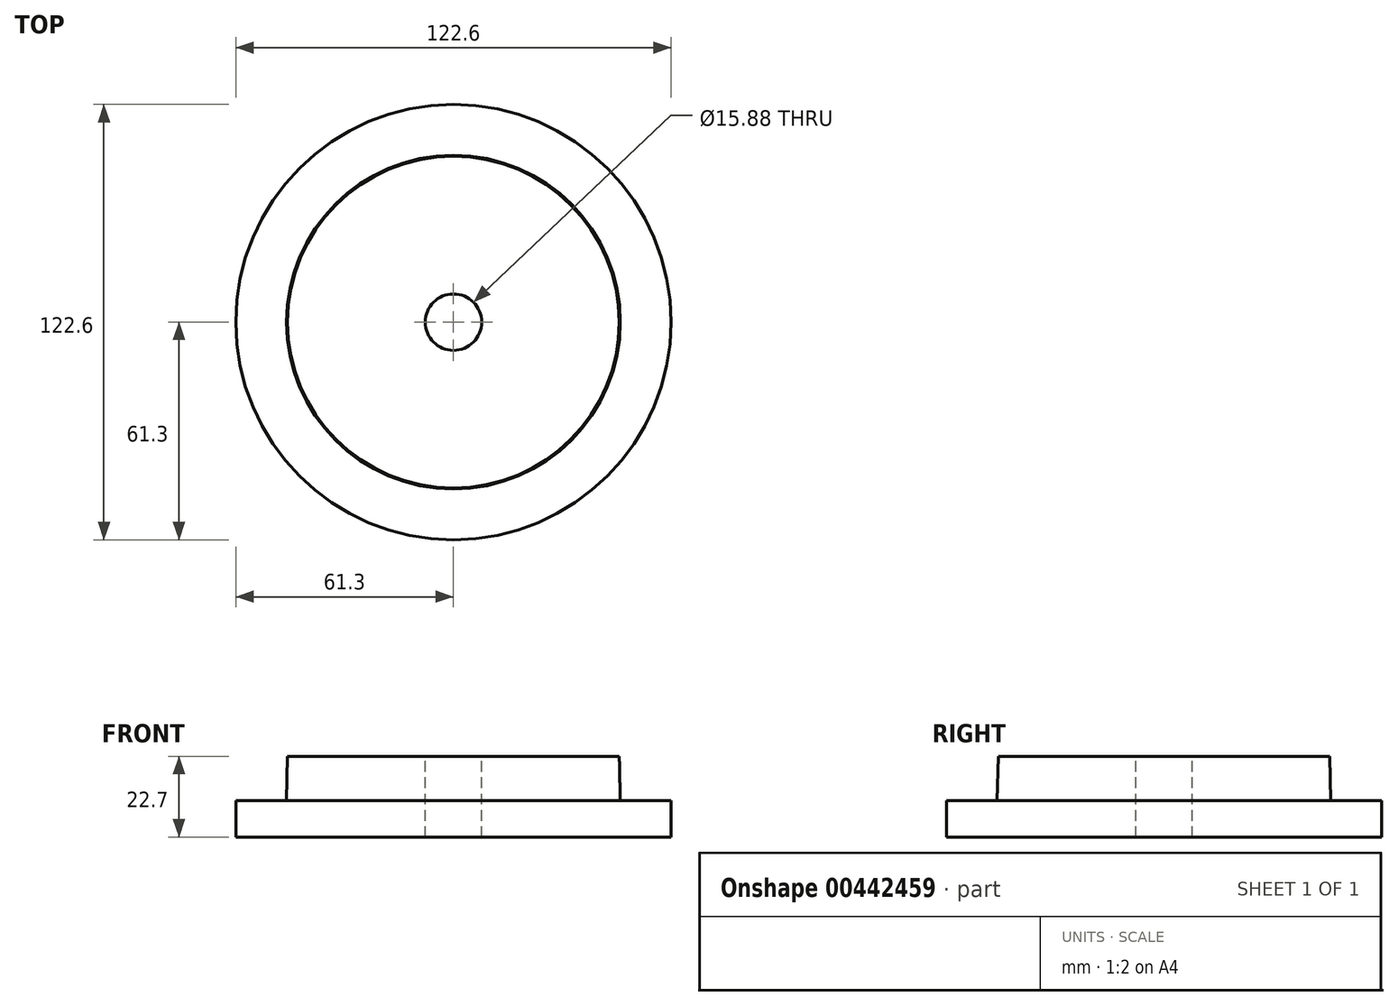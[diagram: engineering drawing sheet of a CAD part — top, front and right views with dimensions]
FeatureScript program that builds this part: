
annotation { "Feature Type Name" : "Feature", "Feature Type Description" : "" }
export const myFeature = defineFeature(function(context is Context, id is Id, definition is map)
    precondition{}
    {
        {
            var Q0;
            Q0=qCreatedBy(makeId("Top.planeOp"),FACE);
            var sketch = newSketch(context, id + "F0", { "sketchPlane" : qUnion([Q0])});
            skCircle(sketch, "E0", {"center": v(0, 0) * mm, "radius": 61.3 * mm});
            skSolve(sketch);
        }
        {
            var Q0;
            Q0 = qSketchRegion(id + "F0", true);
            extrude(context, id + "F1", {"entities" : qUnion([Q0]), "depth" : 10.2 * mm});
        }
        {
            var Q0;
            Q0=makeQuery(id+"F1.opExtrude","CAP_FACE",FACE,{"disambiguationData":[OSD([sQuery(id+"F0.wireOp",EDGE,"E0")])],"isStart":false});
            var sketch = newSketch(context, id + "F2", { "sketchPlane" : qUnion([Q0])});
            skCircle(sketch, "E1", {"center": v(0, 0) * mm, "radius": 47 * mm});
            skSolve(sketch);
        }
        {
            var Q0;
            Q0 = qSketchRegion(id + "F2", true);
            extrude(context, id + "F3", {"entities" : qUnion([Q0]), "operationType" : NewBodyOperationType.ADD, "depth" : 12.5 * mm});
        }
        {
            var Q0;
            Q0=makeQuery(id+"F3.opExtrude","CAP_EDGE",EDGE,{"disambiguationData":[OSD([sQuery(id+"F2.wireOp",EDGE,"E1")])],"isStart":false});
            chamfer(context, id + "F4", {"entities" : qUnion([Q0]), "chamferType" : ChamferType.TWO_OFFSETS, "width1" : .28 * mm, "oppositeDirection" : false, "width2" : 12.5 * mm, "tangentPropagation" : true});
        }
        {
            var Q0;
            Q0=makeQuery(id+"F3.opExtrude","CAP_FACE",FACE,{"disambiguationData":[OSD([sQuery(id+"F2.wireOp",EDGE,"E1")])],"isStart":false});
            var sketch = newSketch(context, id + "F5", { "sketchPlane" : qUnion([Q0])});
            skCircle(sketch, "E2", {"center": v(0, 0) * mm, "radius": 7.94 * mm});
            skSolve(sketch);
        }
        {
            var Q0;
            Q0 = qSketchRegion(id + "F5", true);
            extrude(context, id + "F6", {"entities" : qUnion([Q0]), "operationType" : NewBodyOperationType.REMOVE, "endBound" : BoundingType.THROUGH_ALL, "oppositeDirection" : true, "depth" : 25 * mm});
        }
    });
